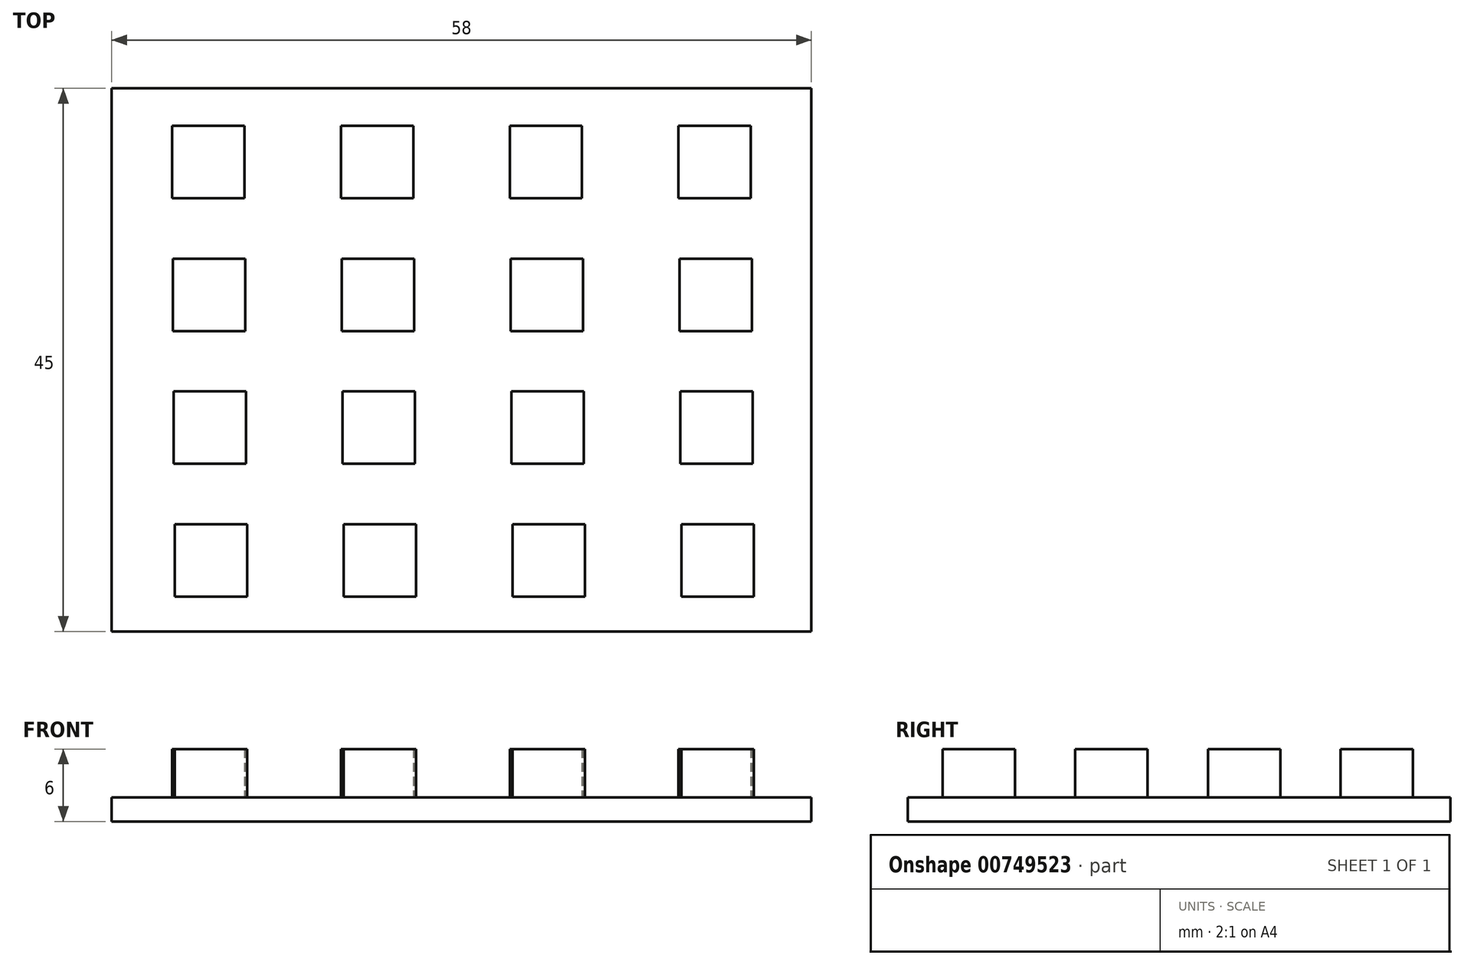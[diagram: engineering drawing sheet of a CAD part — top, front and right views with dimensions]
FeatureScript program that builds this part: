
annotation { "Feature Type Name" : "Feature", "Feature Type Description" : "" }
export const myFeature = defineFeature(function(context is Context, id is Id, definition is map)
    precondition{}
    {
        {
            var Q0;
            Q0=qCreatedBy(makeId("Top.planeOp"),FACE);
            var sketch = newSketch(context, id + "F0", { "sketchPlane" : qUnion([Q0])});
            skLineSegment(sketch, "E0.bottom", {"start": v(-29, 22.5) * mm, "end": v(29, 22.5) * mm});
            skLineSegment(sketch, "E0.top", {"start": v(-29, -22.5) * mm, "end": v(29, -22.5) * mm});
            skLineSegment(sketch, "E0.left", {"start": v(-29, 22.5) * mm, "end": v(-29, -22.5) * mm});
            skLineSegment(sketch, "E0.right", {"start": v(29, 22.5) * mm, "end": v(29, -22.5) * mm});
            skSolve(sketch);
        }
        {
            var Q0;
            Q0=makeQuery(id+"F0.imprint","IMPRINT",FACE,{"disambiguationData":[TD([[makeQuery(id+"F0.imprint","IMPRINT",EDGE,{"derivedFrom":sQuery(id+"F0.wireOp",EDGE,"E0.bottom")}),-1.0]])]});
            extrude(context, id + "F1", {"entities" : qUnion([Q0]), "depth" : 2 * mm, "offsetDistance" : 25 * mm});
        }
        {
            var Q0;
            Q0=makeQuery(id+"F1.opExtrude","CAP_FACE",FACE,{"disambiguationData":[OSD([sQuery(id+"F0.wireOp",EDGE,"E0.bottom"),sQuery(id+"F0.wireOp",EDGE,"E0.top"),sQuery(id+"F0.wireOp",EDGE,"E0.left"),sQuery(id+"F0.wireOp",EDGE,"E0.right")])],"isStart":false});
            var sketch = newSketch(context, id + "F2", { "sketchPlane" : qUnion([Q0])});
            skPoint(sketch, "E1.middle", {"position": v(0, 0) * mm});
            skLineSegment(sketch, "E2.bottom", {"start": v(-18, 13.39) * mm, "end": v(-24, 13.39) * mm});
            skLineSegment(sketch, "E2.top", {"start": v(-18, 19.39) * mm, "end": v(-24, 19.39) * mm});
            skLineSegment(sketch, "E2.left", {"start": v(-18, 13.39) * mm, "end": v(-18, 19.39) * mm});
            skLineSegment(sketch, "E2.right", {"start": v(-24, 13.39) * mm, "end": v(-24, 19.39) * mm});
            skPoint(sketch, "E2.middle", {"position": v(-21, 16.39) * mm});
            skLineSegment(sketch, "E3.1.0.0", {"start": v(-10, 13.39) * mm, "end": v(-10, 19.39) * mm});
            skLineSegment(sketch, "E3.1.0.1", {"start": v(-4, 13.39) * mm, "end": v(-4, 19.39) * mm});
            skLineSegment(sketch, "E3.1.0.2", {"start": v(-4, 19.39) * mm, "end": v(-10, 19.39) * mm});
            skPoint(sketch, "E3.1.0.3", {"position": v(-7, 16.39) * mm});
            skLineSegment(sketch, "E3.1.0.4", {"start": v(-4, 13.39) * mm, "end": v(-10, 13.39) * mm});
            skLineSegment(sketch, "E3.2.0.0", {"start": v(4, 13.39) * mm, "end": v(4, 19.39) * mm});
            skLineSegment(sketch, "E3.2.0.1", {"start": v(10, 13.39) * mm, "end": v(10, 19.39) * mm});
            skLineSegment(sketch, "E3.2.0.2", {"start": v(10, 19.39) * mm, "end": v(4, 19.39) * mm});
            skPoint(sketch, "E3.2.0.3", {"position": v(7, 16.39) * mm});
            skLineSegment(sketch, "E3.2.0.4", {"start": v(10, 13.39) * mm, "end": v(4, 13.39) * mm});
            skLineSegment(sketch, "E3.3.0.0", {"start": v(18, 13.39) * mm, "end": v(18, 19.39) * mm});
            skLineSegment(sketch, "E3.3.0.1", {"start": v(24, 13.39) * mm, "end": v(24, 19.39) * mm});
            skLineSegment(sketch, "E3.3.0.2", {"start": v(24, 19.39) * mm, "end": v(18, 19.39) * mm});
            skPoint(sketch, "E3.3.0.3", {"position": v(21, 16.39) * mm});
            skLineSegment(sketch, "E3.3.0.4", {"start": v(24, 13.39) * mm, "end": v(18, 13.39) * mm});
            skLineSegment(sketch, "E3.direction1", {"start": v(-24, 13.39) * mm, "end": v(-10, 13.39) * mm, "construction": true});
            skLineSegment(sketch, "E4.1.0.0", {"start": v(18.08, 2.39) * mm, "end": v(18.08, 8.39) * mm});
            skLineSegment(sketch, "E4.1.0.1", {"start": v(24.08, 8.39) * mm, "end": v(18.08, 8.39) * mm});
            skLineSegment(sketch, "E4.1.0.2", {"start": v(-23.92, 2.39) * mm, "end": v(-9.92, 2.39) * mm, "construction": true});
            skPoint(sketch, "E4.1.0.3", {"position": v(-20.92, 5.39) * mm});
            skLineSegment(sketch, "E4.1.0.4", {"start": v(4.08, 2.39) * mm, "end": v(4.08, 8.39) * mm});
            skLineSegment(sketch, "E4.1.0.5", {"start": v(-3.92, 2.39) * mm, "end": v(-9.92, 2.39) * mm});
            skLineSegment(sketch, "E4.1.0.6", {"start": v(-3.92, 8.39) * mm, "end": v(-9.92, 8.39) * mm});
            skLineSegment(sketch, "E4.1.0.7", {"start": v(-3.92, 2.39) * mm, "end": v(-3.92, 8.39) * mm});
            skLineSegment(sketch, "E4.1.0.8", {"start": v(-9.92, 2.39) * mm, "end": v(-9.92, 8.39) * mm});
            skLineSegment(sketch, "E4.1.0.9", {"start": v(-23.92, 2.39) * mm, "end": v(-23.92, 8.39) * mm});
            skLineSegment(sketch, "E4.1.0.10", {"start": v(-17.92, 2.39) * mm, "end": v(-17.92, 8.39) * mm});
            skLineSegment(sketch, "E4.1.0.11", {"start": v(-17.92, 8.39) * mm, "end": v(-23.92, 8.39) * mm});
            skPoint(sketch, "E4.1.0.12", {"position": v(7.08, 5.39) * mm});
            skLineSegment(sketch, "E4.1.0.13", {"start": v(10.08, 2.39) * mm, "end": v(4.08, 2.39) * mm});
            skLineSegment(sketch, "E4.1.0.14", {"start": v(10.08, 8.39) * mm, "end": v(4.08, 8.39) * mm});
            skLineSegment(sketch, "E4.1.0.15", {"start": v(10.08, 2.39) * mm, "end": v(10.08, 8.39) * mm});
            skLineSegment(sketch, "E4.1.0.16", {"start": v(24.08, 2.39) * mm, "end": v(24.08, 8.39) * mm});
            skLineSegment(sketch, "E4.1.0.17", {"start": v(24.08, 2.39) * mm, "end": v(18.08, 2.39) * mm});
            skPoint(sketch, "E4.1.0.18", {"position": v(-6.92, 5.39) * mm});
            skPoint(sketch, "E4.1.0.19", {"position": v(21.08, 5.39) * mm});
            skLineSegment(sketch, "E4.1.0.20", {"start": v(-17.92, 2.39) * mm, "end": v(-23.92, 2.39) * mm});
            skLineSegment(sketch, "E4.2.0.0", {"start": v(18.15, -8.61) * mm, "end": v(18.15, -2.61) * mm});
            skLineSegment(sketch, "E4.2.0.1", {"start": v(24.15, -2.61) * mm, "end": v(18.15, -2.61) * mm});
            skLineSegment(sketch, "E4.2.0.2", {"start": v(-23.85, -8.61) * mm, "end": v(-9.85, -8.61) * mm, "construction": true});
            skPoint(sketch, "E4.2.0.3", {"position": v(-20.85, -5.61) * mm});
            skLineSegment(sketch, "E4.2.0.4", {"start": v(4.15, -8.61) * mm, "end": v(4.15, -2.61) * mm});
            skLineSegment(sketch, "E4.2.0.5", {"start": v(-3.85, -8.61) * mm, "end": v(-9.85, -8.61) * mm});
            skLineSegment(sketch, "E4.2.0.6", {"start": v(-3.85, -2.61) * mm, "end": v(-9.85, -2.61) * mm});
            skLineSegment(sketch, "E4.2.0.7", {"start": v(-3.85, -8.61) * mm, "end": v(-3.85, -2.61) * mm});
            skLineSegment(sketch, "E4.2.0.8", {"start": v(-9.85, -8.61) * mm, "end": v(-9.85, -2.61) * mm});
            skLineSegment(sketch, "E4.2.0.9", {"start": v(-23.85, -8.61) * mm, "end": v(-23.85, -2.61) * mm});
            skLineSegment(sketch, "E4.2.0.10", {"start": v(-17.85, -8.61) * mm, "end": v(-17.85, -2.61) * mm});
            skLineSegment(sketch, "E4.2.0.11", {"start": v(-17.85, -2.61) * mm, "end": v(-23.85, -2.61) * mm});
            skPoint(sketch, "E4.2.0.12", {"position": v(7.15, -5.61) * mm});
            skLineSegment(sketch, "E4.2.0.13", {"start": v(10.15, -8.61) * mm, "end": v(4.15, -8.61) * mm});
            skLineSegment(sketch, "E4.2.0.14", {"start": v(10.15, -2.61) * mm, "end": v(4.15, -2.61) * mm});
            skLineSegment(sketch, "E4.2.0.15", {"start": v(10.15, -8.61) * mm, "end": v(10.15, -2.61) * mm});
            skLineSegment(sketch, "E4.2.0.16", {"start": v(24.15, -8.61) * mm, "end": v(24.15, -2.61) * mm});
            skLineSegment(sketch, "E4.2.0.17", {"start": v(24.15, -8.61) * mm, "end": v(18.15, -8.61) * mm});
            skPoint(sketch, "E4.2.0.18", {"position": v(-6.85, -5.61) * mm});
            skPoint(sketch, "E4.2.0.19", {"position": v(21.15, -5.61) * mm});
            skLineSegment(sketch, "E4.2.0.20", {"start": v(-17.85, -8.61) * mm, "end": v(-23.85, -8.61) * mm});
            skLineSegment(sketch, "E4.3.0.0", {"start": v(18.23, -19.61) * mm, "end": v(18.23, -13.61) * mm});
            skLineSegment(sketch, "E4.3.0.1", {"start": v(24.23, -13.61) * mm, "end": v(18.23, -13.61) * mm});
            skLineSegment(sketch, "E4.3.0.2", {"start": v(-23.77, -19.61) * mm, "end": v(-9.77, -19.61) * mm, "construction": true});
            skPoint(sketch, "E4.3.0.3", {"position": v(-20.77, -16.61) * mm});
            skLineSegment(sketch, "E4.3.0.4", {"start": v(4.23, -19.61) * mm, "end": v(4.23, -13.61) * mm});
            skLineSegment(sketch, "E4.3.0.5", {"start": v(-3.77, -19.61) * mm, "end": v(-9.77, -19.61) * mm});
            skLineSegment(sketch, "E4.3.0.6", {"start": v(-3.77, -13.61) * mm, "end": v(-9.77, -13.61) * mm});
            skLineSegment(sketch, "E4.3.0.7", {"start": v(-3.77, -19.61) * mm, "end": v(-3.77, -13.61) * mm});
            skLineSegment(sketch, "E4.3.0.8", {"start": v(-9.77, -19.61) * mm, "end": v(-9.77, -13.61) * mm});
            skLineSegment(sketch, "E4.3.0.9", {"start": v(-23.77, -19.61) * mm, "end": v(-23.77, -13.61) * mm});
            skLineSegment(sketch, "E4.3.0.10", {"start": v(-17.77, -19.61) * mm, "end": v(-17.77, -13.61) * mm});
            skLineSegment(sketch, "E4.3.0.11", {"start": v(-17.77, -13.61) * mm, "end": v(-23.77, -13.61) * mm});
            skPoint(sketch, "E4.3.0.12", {"position": v(7.23, -16.61) * mm});
            skLineSegment(sketch, "E4.3.0.13", {"start": v(10.23, -19.61) * mm, "end": v(4.23, -19.61) * mm});
            skLineSegment(sketch, "E4.3.0.14", {"start": v(10.23, -13.61) * mm, "end": v(4.23, -13.61) * mm});
            skLineSegment(sketch, "E4.3.0.15", {"start": v(10.23, -19.61) * mm, "end": v(10.23, -13.61) * mm});
            skLineSegment(sketch, "E4.3.0.16", {"start": v(24.23, -19.61) * mm, "end": v(24.23, -13.61) * mm});
            skLineSegment(sketch, "E4.3.0.17", {"start": v(24.23, -19.61) * mm, "end": v(18.23, -19.61) * mm});
            skPoint(sketch, "E4.3.0.18", {"position": v(-6.77, -16.61) * mm});
            skPoint(sketch, "E4.3.0.19", {"position": v(21.23, -16.61) * mm});
            skLineSegment(sketch, "E4.3.0.20", {"start": v(-17.77, -19.61) * mm, "end": v(-23.77, -19.61) * mm});
            skLineSegment(sketch, "E4.direction1", {"start": v(-24, 13.39) * mm, "end": v(-23.92, 2.39) * mm, "construction": true});
            skSolve(sketch);
        }
        {
            var Q0;
            Q0=makeQuery(id+"F2.imprint","IMPRINT",FACE,{"disambiguationData":[TD([[makeQuery(id+"F2.imprint","IMPRINT",EDGE,{"derivedFrom":sQuery(id+"F2.wireOp",EDGE,"E2.bottom")}),-1.0]])]});
            var Q1;
            Q1=makeQuery(id+"F2.imprint","IMPRINT",FACE,{"disambiguationData":[TD([[makeQuery(id+"F2.imprint","IMPRINT",EDGE,{"derivedFrom":sQuery(id+"F2.wireOp",EDGE,"E3.1.0.0")}),-1.0]])]});
            var Q2;
            Q2=makeQuery(id+"F2.imprint","IMPRINT",FACE,{"disambiguationData":[TD([[makeQuery(id+"F2.imprint","IMPRINT",EDGE,{"derivedFrom":sQuery(id+"F2.wireOp",EDGE,"E3.2.0.0")}),-1.0]])]});
            var Q3;
            Q3=makeQuery(id+"F2.imprint","IMPRINT",FACE,{"disambiguationData":[TD([[makeQuery(id+"F2.imprint","IMPRINT",EDGE,{"derivedFrom":sQuery(id+"F2.wireOp",EDGE,"E3.3.0.0")}),-1.0]])]});
            var Q4;
            Q4=makeQuery(id+"F2.imprint","IMPRINT",FACE,{"disambiguationData":[TD([[makeQuery(id+"F2.imprint","IMPRINT",EDGE,{"derivedFrom":sQuery(id+"F2.wireOp",EDGE,"E4.1.0.9")}),-1.0]])]});
            var Q5;
            Q5=makeQuery(id+"F2.imprint","IMPRINT",FACE,{"disambiguationData":[TD([[makeQuery(id+"F2.imprint","IMPRINT",EDGE,{"derivedFrom":sQuery(id+"F2.wireOp",EDGE,"E4.1.0.5")}),-1.0]])]});
            var Q6;
            Q6=makeQuery(id+"F2.imprint","IMPRINT",FACE,{"disambiguationData":[TD([[makeQuery(id+"F2.imprint","IMPRINT",EDGE,{"derivedFrom":sQuery(id+"F2.wireOp",EDGE,"E4.1.0.4")}),-1.0]])]});
            var Q7;
            Q7=makeQuery(id+"F2.imprint","IMPRINT",FACE,{"disambiguationData":[TD([[makeQuery(id+"F2.imprint","IMPRINT",EDGE,{"derivedFrom":sQuery(id+"F2.wireOp",EDGE,"E4.1.0.0")}),-1.0]])]});
            var Q8;
            Q8=makeQuery(id+"F2.imprint","IMPRINT",FACE,{"disambiguationData":[TD([[makeQuery(id+"F2.imprint","IMPRINT",EDGE,{"derivedFrom":sQuery(id+"F2.wireOp",EDGE,"E4.2.0.9")}),-1.0]])]});
            var Q9;
            Q9=makeQuery(id+"F2.imprint","IMPRINT",FACE,{"disambiguationData":[TD([[makeQuery(id+"F2.imprint","IMPRINT",EDGE,{"derivedFrom":sQuery(id+"F2.wireOp",EDGE,"E4.2.0.5")}),-1.0]])]});
            var Q10;
            Q10=makeQuery(id+"F2.imprint","IMPRINT",FACE,{"disambiguationData":[TD([[makeQuery(id+"F2.imprint","IMPRINT",EDGE,{"derivedFrom":sQuery(id+"F2.wireOp",EDGE,"E4.2.0.4")}),-1.0]])]});
            var Q11;
            Q11=makeQuery(id+"F2.imprint","IMPRINT",FACE,{"disambiguationData":[TD([[makeQuery(id+"F2.imprint","IMPRINT",EDGE,{"derivedFrom":sQuery(id+"F2.wireOp",EDGE,"E4.2.0.0")}),-1.0]])]});
            var Q12;
            Q12=makeQuery(id+"F2.imprint","IMPRINT",FACE,{"disambiguationData":[TD([[makeQuery(id+"F2.imprint","IMPRINT",EDGE,{"derivedFrom":sQuery(id+"F2.wireOp",EDGE,"E4.3.0.9")}),-1.0]])]});
            var Q13;
            Q13=makeQuery(id+"F2.imprint","IMPRINT",FACE,{"disambiguationData":[TD([[makeQuery(id+"F2.imprint","IMPRINT",EDGE,{"derivedFrom":sQuery(id+"F2.wireOp",EDGE,"E4.3.0.5")}),-1.0]])]});
            var Q14;
            Q14=makeQuery(id+"F2.imprint","IMPRINT",FACE,{"disambiguationData":[TD([[makeQuery(id+"F2.imprint","IMPRINT",EDGE,{"derivedFrom":sQuery(id+"F2.wireOp",EDGE,"E4.3.0.4")}),-1.0]])]});
            var Q15;
            Q15=makeQuery(id+"F2.imprint","IMPRINT",FACE,{"disambiguationData":[TD([[makeQuery(id+"F2.imprint","IMPRINT",EDGE,{"derivedFrom":sQuery(id+"F2.wireOp",EDGE,"E4.3.0.0")}),-1.0]])]});
            extrude(context, id + "F3", {"entities" : qUnion([Q0, Q1, Q2, Q3, Q4, Q5, Q6, Q7, Q8, Q9, Q10, Q11, Q12, Q13, Q14, Q15]), "operationType" : NewBodyOperationType.ADD, "depth" : 4 * mm, "offsetDistance" : 25 * mm});
        }
    });
